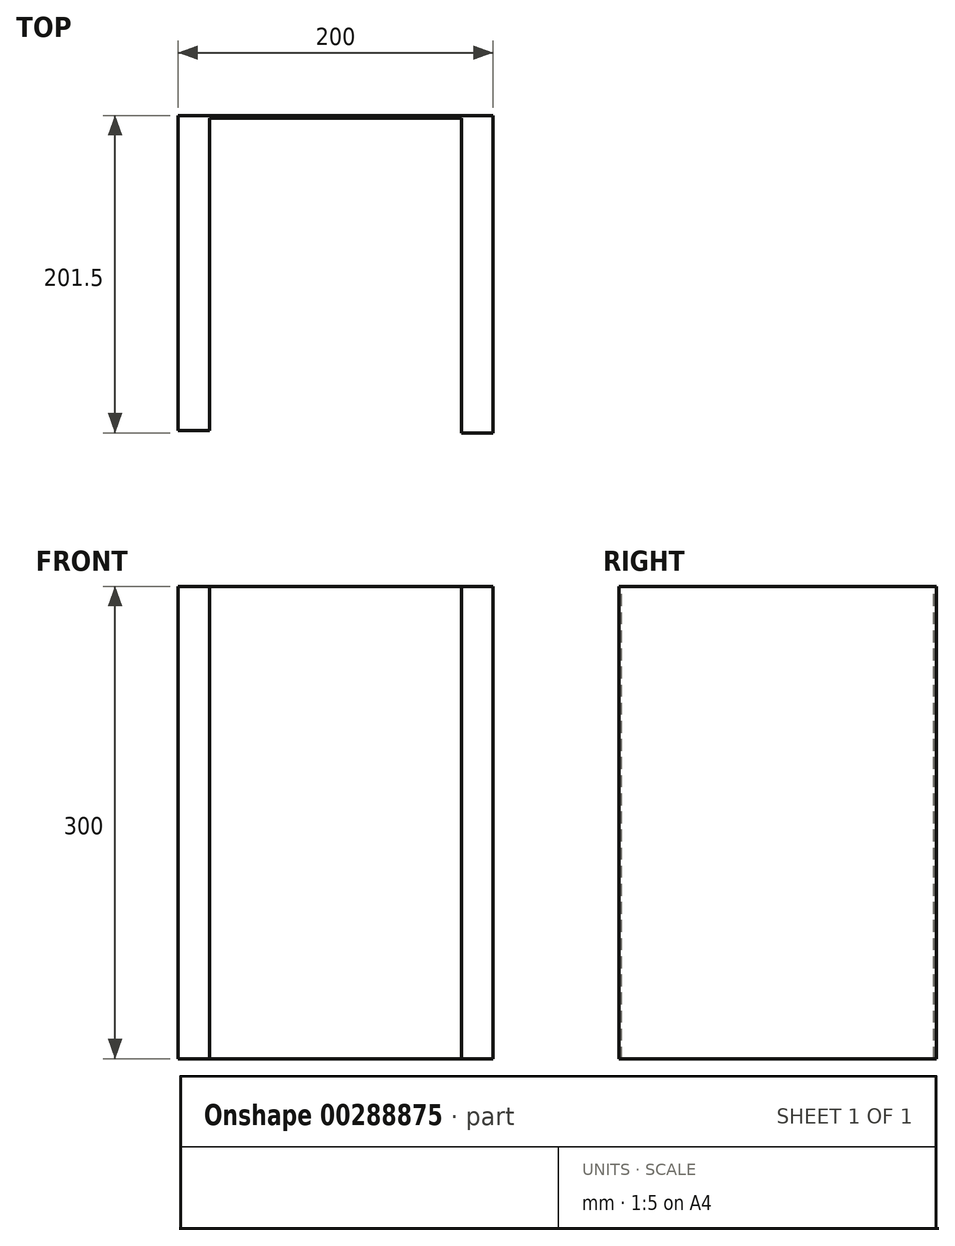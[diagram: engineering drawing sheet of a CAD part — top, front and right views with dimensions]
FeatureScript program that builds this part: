
annotation { "Feature Type Name" : "Feature", "Feature Type Description" : "" }
export const myFeature = defineFeature(function(context is Context, id is Id, definition is map)
    precondition{}
    {
        {
            var Q0;
            Q0=qCreatedBy(makeId("Front.planeOp"),FACE);
            var sketch = newSketch(context, id + "F0", { "sketchPlane" : qUnion([Q0])});
            skLineSegment(sketch, "E0.bottom", {"start": v(0, 0) * mm, "end": v(200, 0) * mm});
            skLineSegment(sketch, "E0.top", {"start": v(0, 300) * mm, "end": v(200, 300) * mm});
            skLineSegment(sketch, "E0.left", {"start": v(0, 0) * mm, "end": v(0, 300) * mm});
            skLineSegment(sketch, "E0.right", {"start": v(200, 0) * mm, "end": v(200, 300) * mm});
            skSolve(sketch);
        }
        {
            var Q0;
            Q0 = qSketchRegion(id + "F0", true);
            extrude(context, id + "F1", {"entities" : qUnion([Q0]), "depth" : 1.5 * mm});
        }
        {
            var Q0;
            Q0=qCreatedBy(makeId("Front.planeOp"),FACE);
            var sketch = newSketch(context, id + "F2", { "sketchPlane" : qUnion([Q0])});
            skLineSegment(sketch, "E1.bottom", {"start": v(0, 0) * mm, "end": v(20, 0) * mm});
            skLineSegment(sketch, "E1.top", {"start": v(0, 300) * mm, "end": v(20, 300) * mm});
            skLineSegment(sketch, "E1.left", {"start": v(0, 0) * mm, "end": v(0, 300) * mm});
            skLineSegment(sketch, "E1.right", {"start": v(20, 0) * mm, "end": v(20, 300) * mm});
            skSolve(sketch);
        }
        {
            var Q0;
            Q0 = qSketchRegion(id + "F2", true);
            extrude(context, id + "F3", {"entities" : qUnion([Q0]), "operationType" : NewBodyOperationType.ADD, "depth" : 200 * mm});
        }
        {
            var Q0;
            Q0=makeQuery(id+"F1.opExtrude","CAP_FACE",FACE,{"disambiguationData":[OSD([sQuery(id+"F0.wireOp",EDGE,"E0.bottom"),sQuery(id+"F0.wireOp",EDGE,"E0.top"),sQuery(id+"F0.wireOp",EDGE,"E0.left"),sQuery(id+"F0.wireOp",EDGE,"E0.right")])],"isStart":false});
            var sketch = newSketch(context, id + "F4", { "sketchPlane" : qUnion([Q0])});
            skLineSegment(sketch, "E2.bottom", {"start": v(200, 0) * mm, "end": v(180, 0) * mm});
            skLineSegment(sketch, "E2.top", {"start": v(200, 300) * mm, "end": v(180, 300) * mm});
            skLineSegment(sketch, "E2.left", {"start": v(200, 0) * mm, "end": v(200, 300) * mm});
            skLineSegment(sketch, "E2.right", {"start": v(180, 0) * mm, "end": v(180, 300) * mm});
            skSolve(sketch);
        }
        {
            var Q0;
            Q0=makeQuery(id+"F4.imprint","IMPRINT",FACE,{"disambiguationData":[TD([[makeQuery(id+"F4.imprint","IMPRINT",EDGE,{"derivedFrom":sQuery(id+"F4.wireOp",EDGE,"E2.bottom")}),1.0]])]});
            extrude(context, id + "F5", {"entities" : qUnion([Q0]), "operationType" : NewBodyOperationType.ADD, "depth" : 200 * mm});
        }
    });
